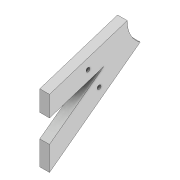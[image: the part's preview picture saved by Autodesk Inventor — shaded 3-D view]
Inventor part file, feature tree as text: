
AUTODESK INVENTOR PART (.ipt)
format: ipt  version: 2022 (Build 260153000, 153)  size: 275,456 bytes
history: native  units: mm
features: sketch x4, extrude x3, projected_geometry x1
ambient origin geometry x8: Origin, YZ Plane, XZ Plane, XY Plane, X Axis, Y Axis, Z Axis, Center Point
bodies: Solid1 (feature_tree)
feature tree (8):
  extrude  "Extrusion1"  Depth=3.9mm
  sketch  "Sketch8"  dims[d6=5.0mm d7=0.0mm d25=3.0mm]
  extrude  "Extrusion4"  Depth=5.0mm
  extrude  "Extrusion5"  Depth=59.0mm
  sketch  "Sketch1"  dims[d2=3.9mm d4=3.9mm]
  sketch  "Sketch9"  dims[d28=3.0mm d43=59.0mm]
  sketch  "Sketch10"  dims[d44=65.0mm d45=65.0mm d47=59.0mm d48=10.0mm d49=10.0mm d50=10.0mm d52=14.0mm d53=3.0mm d54=3.0mm d55=4.0mm d56=4.0mm d57=25.0mm d58=25.0mm d59=10.0mm d60=10.0mm d61=5.0mm d62=3.0mm d63=3.0mm d64=3.0mm d65=3.0mm d66=3.0mm d67=10.0mm d68=25.0mm d69=3.0mm d70=3.0mm d71=10.0mm d72=25.0mm d73=25.0mm d74=25.0mm d76=2.0mm d78=2.0mm d79=2.0mm d80=2.0mm d81=6.0mm d82=6.0mm d83=2.0mm d84=30.0mm d85=4.0mm d86=5.0mm d87=0.0mm d88=10.0mm d89=0.0mm]
  projected_geometry  "Project Cut Edges1"
